# Revit family: SL1
name_source: partatom
category: Lighting Fixtures
units: mm (PartAtom-declared; Revit-internal decimal feet)

## family parameters
Always vertical = Yes
Cut with Voids When Loaded = No
Light Source = Yes
OmniClass Number = 23.80.70.14
OmniClass Title = Luminaries for External Lighting
Part Type = Normal
Room Calculation Point = No
Round Connector Dimension = Use Diameter
Shared = No
Work Plane-Based = Yes

## types (1)
- SL1
    Apparent Load = 56 VA
    Assembly Code = D5020200
    Color Filter = 16777215
    Default Elevation = 48 "
    Description = Sight Lightforms are specifically designed and engineered to combine contemporary form with rugged vandal-resistant construction. All fixture heads are heavy-wall one-piece aluminum castings and head to shaft connections are concealed for greater strength and clean detailing.
    Diameter = 5 "
    Dimming Lamp Color Temperature Shift = <None>
    Emit Shape Visible in Rendering = No
    Emit from Rectangle Length = 4 "
    Emit from Rectangle Width = 4 "
    Finish = Powder Coat-White
    Glass = Glass-Temper Molded
    Height = 24 "
    Lamp = LED
    Load Classification = Lighting
    Manufacturer = Kim Lighting
    MasterFormat Title = Landscape Lighting, Site Lighting, Walkway Lighting
    Model = Site Lightforms
    Number of Poles = 1
    Photometric Notes = More IES files download on Photometric Web Link
    Photometric Web File = sl1-36l3k.ies
    Power Factor = 1
    Radius = 2.5 "
    Series = Site Lightforms
    Tilt Angle = 60.00°
    Type Comments = Light Fixture
    URL = https://www.currentlighting.com
    Voltage = 120 V
    Wattage Comments = default

## geometry (parser evidence)
native form markers: Sweep x4
no freeform markers — native parametric forms only
